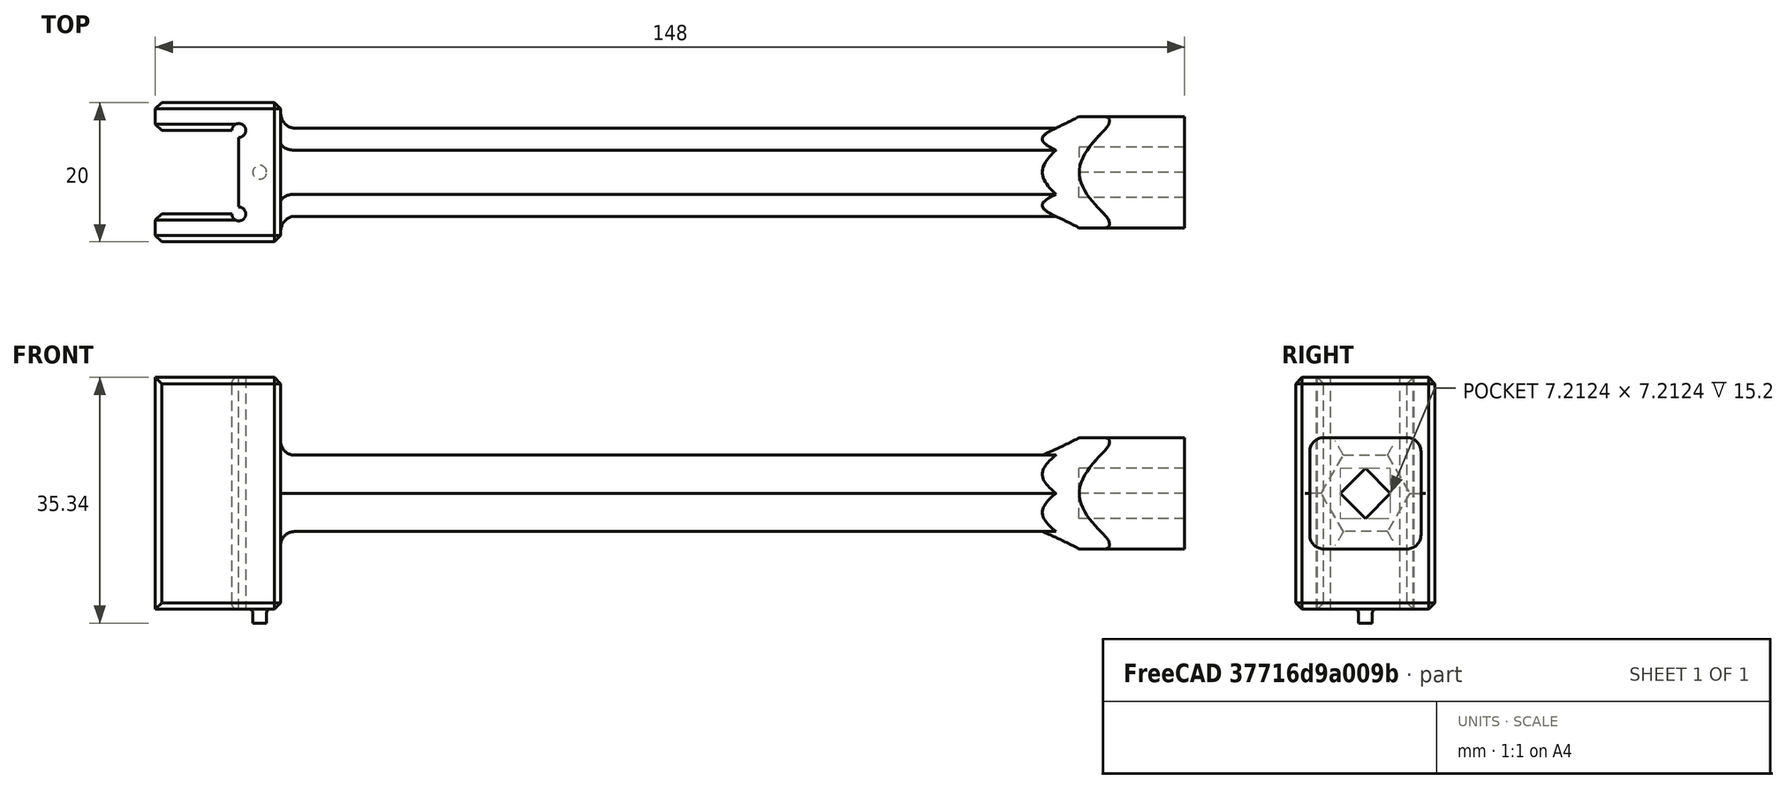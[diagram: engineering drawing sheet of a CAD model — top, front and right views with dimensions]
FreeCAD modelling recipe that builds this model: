
FCSTD DOCUMENT  (FreeCAD 0.21R33771 (Git))
Label: wrench
License: All rights reserved
LicenseURL: http://en.wikipedia.org/wiki/All_rights_reserved
objects: Sketcher::SketchObject×8, PartDesign::Pad×4, PartDesign::Fillet×3, PartDesign::Pocket×3, Spreadsheet::Sheet×1, PartDesign::Plane×1, PartDesign::Revolution×1, PartDesign::Chamfer×1, PartDesign::Body×1, Mesh::Feature×1
note: 34 computed .brp shape members not serialized (recipe doc carries the construction recipe); baked Part::Feature solids carry a one-line shape summary decoded from their .brp

FEATURE [Spreadsheet::Sheet] Spreadsheet
  cells = A1='magnet width [mm]; B1=12; A2='manget lenght [mm]; B2=50; A3='holder wall thickness; B3=2
FEATURE [Sketcher::SketchObject] Sketch
  FullyConstrained = false
  MapMode = 5
  Support = -> [XY_Plane]
  expr: Constraints[13] = Spreadsheet.B1 / 3
  expr: Constraints[15] = Spreadsheet.B1
  expr: Constraints[25] = Spreadsheet.B1 / 2
  sketch-geometry (21):
    g0: LineSegment StartX=-6 StartY=6 StartZ=0 EndX=-6 EndY=10 EndZ=0
    g1: LineSegment StartX=-6 StartY=10 StartZ=0 EndX=12 EndY=10 EndZ=0
    g2: LineSegment StartX=12 StartY=10 StartZ=0 EndX=12 EndY=-10 EndZ=0
    g3: LineSegment StartX=12 StartY=-10 StartZ=0 EndX=-6 EndY=-10 EndZ=0
    g4: LineSegment StartX=-6 StartY=-10 StartZ=0 EndX=-6 EndY=-6 EndZ=0
    g5: LineSegment StartX=-6 StartY=-6 StartZ=0 EndX=6 EndY=-6 EndZ=0
    g6: LineSegment StartX=6 StartY=-6 StartZ=0 EndX=6 EndY=6 EndZ=0
    g7: LineSegment StartX=6 StartY=6 StartZ=0 EndX=-6 EndY=6 EndZ=0
    g8: LineSegment StartX=-6 StartY=6 StartZ=0 EndX=6 EndY=-6 EndZ=0
    g9: LineSegment StartX=6 StartY=6 StartZ=0 EndX=-6 EndY=-6 EndZ=0
    g10: LineSegment StartX=-6 StartY=6 StartZ=0 EndX=5.2 EndY=6 EndZ=0
    g11: LineSegment StartX=6 StartY=6 StartZ=0 EndX=6 EndY=-6 EndZ=0
    g12: LineSegment StartX=-6 StartY=-6 StartZ=0 EndX=5.2 EndY=-6 EndZ=0
    g13: LineSegment StartX=-6 StartY=-6 StartZ=0 EndX=-3 EndY=-6 EndZ=0
    g14: LineSegment StartX=-6 StartY=-7 StartZ=0 EndX=-6 EndY=-6 EndZ=0
    g15: LineSegment StartX=-6 StartY=6 StartZ=0 EndX=-3 EndY=6 EndZ=0
    g16: LineSegment StartX=-6 StartY=7 StartZ=0 EndX=-6 EndY=6 EndZ=0
    g17: LineSegment StartX=-6 StartY=6 StartZ=0 EndX=-6 EndY=10 EndZ=0
    g18: LineSegment StartX=-6 StartY=-6 StartZ=0 EndX=-6 EndY=-10 EndZ=0
    g19: LineSegment StartX=-6 StartY=6 StartZ=0 EndX=6 EndY=6 EndZ=0
    g20: LineSegment StartX=-6 StartY=-6 StartZ=0 EndX=6 EndY=-6 EndZ=0
  constraints (49):
    c: Coincident(g1,g0)
    c: Horizontal(g1)
    c: Coincident(g2,g1)
    c: Vertical(g2)
    c: Coincident(g3,g2)
    c: Horizontal(g3)
    c: Coincident(g4,g3)
    c: Coincident(g5,g4)
    c: Horizontal(g5)
    c: Coincident(g7,g0)
    c: Horizontal(g7)
    c: Coincident(g5,g6)
    c: Coincident(g6,g7)
    c: Distance(g6,g1) = 4
    c: Equal(g0,g4)
    c: Distance(g4,g7) = 12
    c: Coincident(g8,g0)
    c: Coincident(g8,g5)
    c: PointOnObject(g-1,g8)
    c: Tangent(g0,g4)
    c: Vertical(g0)
    c: Coincident(g9,g6)
    c: Coincident(g9,g4)
    c: PointOnObject(g-1,g9)
    c: Equal(g7,g6)
    c: Distance(g5,g2) = 6
    c: Coincident(g10,g0)
    c: PointOnObject(g10,g7)
    c: Coincident(g12,g4)
    c: PointOnObject(g12,g5)
    c: Coincident(g14,g13)
    c: Horizontal(g13)
    c: Vertical(g14)
    c: Coincident(g13,g4)
    c: Coincident(g16,g15)
    c: Horizontal(g15)
    c: Vertical(g16)
    c: Coincident(g15,g0)
    c: Coincident(g17,g1)
    c: Coincident(g18,g3)
    c: Coincident(g17,g0)
    c: Coincident(g19,g17)
    c: Coincident(g18,g4)
    c: Coincident(g20,g18)
    c: Coincident(g19,g6)
    c: Coincident(g11,g19)
    c: Coincident(g20,g5)
    c: Coincident(g11,g20)
    c: Vertical(g11)
FEATURE [PartDesign::Pad] Pad  label="wrench"
  Direction = (0,0,1)
  Length = 16.6667
  Length2 = 16.6667
  Profile = -> Sketch
  ReferenceAxis = -> Sketch [N_Axis]
  Type = 4
  expr: Length = Spreadsheet.B2 * 2 / 6
  expr: Length2 = Spreadsheet.B2 * 2 / 6
FEATURE [PartDesign::Plane] DatumPlane
  AttachmentOffset = pos=(0,0,7) rot=(0,0,1;0rad)
  Length = 60
  MapMode = 5
  Placement = pos=(7,-1.6e-15,1.6e-15) rot=(0.57735,0.57735,0.57735;2.0944rad)
  ResizeMode = 0
  Support = -> [YZ_Plane]
  Width = 60
  expr: .AttachmentOffset.Base.z = Spreadsheet.B1 / 2 + 1
FEATURE [Sketcher::SketchObject] Sketch001
  FullyConstrained = true
  MapMode = 5
  Placement = pos=(7,-1.6e-15,1.6e-15) rot=(0.57735,0.57735,0.57735;2.0944rad)
  Support = -> [DatumPlane]
  sketch-geometry (7):
    g0: LineSegment StartX=3.17543 StartY=5.5 StartZ=0 EndX=-3.17543 EndY=5.5 EndZ=0
    g1: LineSegment StartX=-3.17543 StartY=5.5 StartZ=0 EndX=-6.35085 EndY=0 EndZ=0
    g2: LineSegment StartX=-6.35085 StartY=0 StartZ=0 EndX=-3.17543 EndY=-5.5 EndZ=0
    g3: LineSegment StartX=-3.17543 StartY=-5.5 StartZ=0 EndX=3.17543 EndY=-5.5 EndZ=0
    g4: LineSegment StartX=3.17543 StartY=-5.5 StartZ=0 EndX=6.35085 EndY=-9e-16 EndZ=0
    g5: LineSegment StartX=6.35085 StartY=-9e-16 StartZ=0 EndX=3.17543 EndY=5.5 EndZ=0
    g6: Circle CenterX=0 CenterY=0 CenterZ=0 NormalX=0 NormalY=0 NormalZ=1 AngleXU=0 Radius=6.35085
  constraints (16):
    c: Coincident(g0,g1)
    c: Coincident(g1,g2)
    c: Coincident(g2,g3)
    c: Coincident(g3,g4)
    c: Coincident(g4,g5)
    c: Coincident(g5,g0)
    c: Equal(g0, g1-g5) x5
    c: PointOnObject(g0,g6)
    c: PointOnObject(g1,g6)
    c: PointOnObject(g2,g6)
    c: PointOnObject(g3,g6)
    c: PointOnObject(g4,g6)
    c: PointOnObject(g5,g6)
    c: Horizontal(g0)
    c: Distance(g0,g3) = 11
    c: Coincident(g6,g-1)
FEATURE [PartDesign::Pad] Pad001  label="handle"
  BaseFeature = -> Pad
  Direction = (1,-1e-16,1e-16)
  Length = 130
  Length2 = 10
  Profile = -> Sketch001
  ReferenceAxis = -> Sketch001 [N_Axis]
  Type = 0
FEATURE [Sketcher::SketchObject] Sketch005
  FullyConstrained = false
  MapMode = 5
  Support = -> [XY_Plane]
  expr: Constraints[2] = Spreadsheet.B1 * sqrt(2) / 2 + Spreadsheet.B3 + 4
  sketch-geometry (5):
    g0: LineSegment StartX=137 StartY=0 StartZ=0 EndX=137 EndY=14.4853 EndZ=0
    g1: LineSegment StartX=137 StartY=14.4853 StartZ=0 EndX=94.3606 EndY=70 EndZ=0
    g2: ArcOfCircle CenterX=94.3606 CenterY=70 CenterZ=0 NormalX=0 NormalY=0 NormalZ=1 AngleXU=0 Radius=70 StartAngle=4.71239 EndAngle=5.36736
    g3: LineSegment StartX=94.3606 StartY=0 StartZ=0 EndX=94.3606 EndY=70 EndZ=0
    g4: LineSegment StartX=94.3606 StartY=0 StartZ=0 EndX=137 EndY=0 EndZ=0
  constraints (13):
    c: Vertical(g0)
    c: PointOnObject(g0,g-1)
    c: DistanceY(g0,g0) = 14.4853
    c: Coincident(g1,g0)
    c: Coincident(g2,g1)
    c: Coincident(g2,g0)
    c: Coincident(g3,g2)
    c: Coincident(g3,g2)
    c: Coincident(g4,g2)
    c: Coincident(g4,g0)
    c: Horizontal(g4)
    c: Vertical(g3)
    c: DistanceY(g2) = 70
FEATURE [Sketcher::SketchObject] Sketch002
  FullyConstrained = true
  MapMode = 5
  Placement = pos=(137,0,2.2e-14) rot=(0.57735,0.57735,0.57735;2.0944rad)
  expr: Constraints[10] = Spreadsheet.B1 + Spreadsheet.B3 * 2
  sketch-geometry (5):
    g0: LineSegment StartX=-8 StartY=-8 StartZ=0 EndX=-8 EndY=8 EndZ=0
    g1: LineSegment StartX=-8 StartY=8 StartZ=0 EndX=8 EndY=8 EndZ=0
    g2: LineSegment StartX=8 StartY=8 StartZ=0 EndX=8 EndY=-8 EndZ=0
    g3: LineSegment StartX=8 StartY=-8 StartZ=0 EndX=-8 EndY=-8 EndZ=0
    g4: GeomPoint X=0 Y=0 Z=0
  constraints (12):
    c: Coincident(g0,g1)
    c: Coincident(g1,g2)
    c: Coincident(g2,g3)
    c: Coincident(g3,g0)
    c: Horizontal(g1)
    c: Horizontal(g3)
    c: Vertical(g0)
    c: Vertical(g2)
    c: Symmetric(g1,g0,g4)
    c: Coincident(g4,g-1)
    c: Distance(g1,g2) = 16
    c: Equal(g2,g3)
FEATURE [PartDesign::Pad] Pad002  label="holder body"
  BaseFeature = -> Pad001
  Direction = (1,0,0)
  Length = 5
  Length2 = 10
  Profile = -> Sketch002
  ReferenceAxis = -> Sketch002 [N_Axis]
  Type = 0
FEATURE [PartDesign::Fillet] Fillet001  label="wrench fillets"
  Base = -> Pad002 [Edge24,Edge26,Edge28,Edge30,Edge19,Edge22]
  BaseFeature = -> Pad002
  Radius = 2
  SupportTransform = false
  UseAllEdges = false
FEATURE [PartDesign::Fillet] Fillet002  label="holder outer fillets"
  Base = -> Fillet001 [Edge37,Edge39,Edge34,Edge35]
  BaseFeature = -> Fillet001
  Radius = 2
  SupportTransform = false
  UseAllEdges = false
  expr: Radius = Spreadsheet.B3
FEATURE [PartDesign::Revolution] Revolution  label="rounden rod to holder"
  Angle = 360
  Axis = (1,0,0)
  Base = (0,0,0)
  BaseFeature = -> Fillet002
  Profile = -> Sketch005
  ReferenceAxis = -> Sketch005 [H_Axis]
FEATURE [Sketcher::SketchObject] Sketch006
  FullyConstrained = false
  MapMode = 5
  Placement = pos=(137,0,0) rot=(0.57735,0.57735,0.57735;2.0944rad)
  Support = -> [Revolution]
  expr: Constraints[22] = Spreadsheet.B1 + Spreadsheet.B3 * 2
  expr: Constraints[34] = Spreadsheet.B1 + Spreadsheet.B3 * 2 - 4
  sketch-geometry (23):
    g0: LineSegment StartX=-35 StartY=-35 StartZ=0 EndX=-35 EndY=35 EndZ=0
    g1: LineSegment StartX=-35 StartY=35 StartZ=0 EndX=35 EndY=35 EndZ=0
    g2: LineSegment StartX=35 StartY=35 StartZ=0 EndX=35 EndY=-35 EndZ=0
    g3: LineSegment StartX=35 StartY=-35 StartZ=0 EndX=-35 EndY=-35 EndZ=0
    g4: GeomPoint X=0 Y=0 Z=0
    g5: LineSegment StartX=-8 StartY=-8 StartZ=0 EndX=-8 EndY=8 EndZ=0
    g6: LineSegment StartX=-8 StartY=8 StartZ=0 EndX=8 EndY=8 EndZ=0
    g7: LineSegment StartX=8 StartY=8 StartZ=0 EndX=8 EndY=-8 EndZ=0
    g8: LineSegment StartX=8 StartY=-8 StartZ=0 EndX=-8 EndY=-8 EndZ=0
    g9: GeomPoint X=0 Y=0 Z=0
    g10: LineSegment StartX=-6 StartY=-6 StartZ=0 EndX=-6 EndY=6 EndZ=0
    g11: LineSegment StartX=-6 StartY=6 StartZ=0 EndX=6 EndY=6 EndZ=0
    g12: LineSegment StartX=6 StartY=6 StartZ=0 EndX=6 EndY=-6 EndZ=0
    g13: LineSegment StartX=6 StartY=-6 StartZ=0 EndX=-6 EndY=-6 EndZ=0
    g14: GeomPoint X=0 Y=0 Z=0
    g15: ArcOfCircle CenterX=-6 CenterY=6 CenterZ=0 NormalX=0 NormalY=0 NormalZ=1 AngleXU=0 Radius=2 StartAngle=1.5708 EndAngle=3.14159
    g16: ArcOfCircle CenterX=6 CenterY=6 CenterZ=0 NormalX=0 NormalY=0 NormalZ=1 AngleXU=0 Radius=2 StartAngle=2.09637e-08 EndAngle=1.5708
    g17: ArcOfCircle CenterX=6 CenterY=-6 CenterZ=0 NormalX=0 NormalY=0 NormalZ=1 AngleXU=0 Radius=2 StartAngle=4.71239 EndAngle=6.28319
    g18: ArcOfCircle CenterX=-6 CenterY=-6 CenterZ=0 NormalX=0 NormalY=0 NormalZ=1 AngleXU=0 Radius=2 StartAngle=3.14159 EndAngle=4.71239
    g19: LineSegment StartX=-6 StartY=8 StartZ=0 EndX=6 EndY=8 EndZ=0
    g20: LineSegment StartX=8 StartY=6 StartZ=0 EndX=8 EndY=-6 EndZ=0
    g21: LineSegment StartX=6 StartY=-8 StartZ=0 EndX=-6 EndY=-8 EndZ=0
    g22: LineSegment StartX=-8 StartY=-6 StartZ=0 EndX=-8 EndY=6 EndZ=0
  constraints (55):
    c: Coincident(g0,g1)
    c: Coincident(g1,g2)
    c: Coincident(g2,g3)
    c: Coincident(g3,g0)
    c: Horizontal(g1)
    c: Horizontal(g3)
    c: Vertical(g0)
    c: Vertical(g2)
    c: Symmetric(g1,g0,g4)
    c: Coincident(g4,g-1)
    c: Equal(g2,g3)
    c: Distance(g1,g2) = 70
    c: Coincident(g5,g6)
    c: Coincident(g6,g7)
    c: Coincident(g7,g8)
    c: Coincident(g8,g5)
    c: Horizontal(g8)
    c: Vertical(g5)
    c: Vertical(g7)
    c: Symmetric(g6,g5,g9)
    c: Coincident(g9,g4)
    c: Equal(g7,g8)
    c: Distance(g6,g7) = 16
    c: Coincident(g10,g11)
    c: Coincident(g11,g12)
    c: Coincident(g12,g13)
    c: Coincident(g13,g10)
    c: Horizontal(g11)
    c: Horizontal(g13)
    c: Vertical(g10)
    c: Vertical(g12)
    c: Symmetric(g11,g10,g14)
    c: Coincident(g14,g4)
    c: Equal(g12,g13)
    c: Distance(g11,g12) = 12
    c: Coincident(g15,g10)
    c: PointOnObject(g15,g6)
    c: Tangent(g15,g5) = 1.5708
    c: Coincident(g16,g11)
    c: PointOnObject(g16,g7)
    c: Tangent(g16,g6) = 1.5708
    c: Coincident(g17,g12)
    c: PointOnObject(g17,g8)
    c: Tangent(g17,g7) = 1.5708
    c: Tangent(g18,g8) = 1.5708
    c: Coincident(g18,g10)
    c: Coincident(g19,g15)
    c: Coincident(g19,g16)
    c: Coincident(g20,g16)
    c: Vertical(g20)
    c: Coincident(g21,g17)
    c: Coincident(g21,g18)
    c: Coincident(g22,g18)
    c: Vertical(g22)
    c: Coincident(g22,g15)
FEATURE [PartDesign::Pocket] Pocket002  label="cut down to holder"
  BaseFeature = -> Revolution
  Direction = (-1,0,0)
  Length = 21
  Length2 = 5
  Profile = -> Sketch006
  ReferenceAxis = -> Sketch006 [N_Axis]
  Type = 0
FEATURE [Sketcher::SketchObject] Sketch007
  FullyConstrained = true
  MapMode = 5
  Placement = pos=(142,0,0) rot=(0.57735,0.57735,0.57735;2.0944rad)
  Support = -> [Pocket002]
  sketch-geometry (13):
    g0: LineSegment StartX=3.17543 StartY=5.5 StartZ=0 EndX=-3.17543 EndY=5.5 EndZ=0
    g1: LineSegment StartX=-3.17543 StartY=5.5 StartZ=0 EndX=-6.35085 EndY=1.40936e-11 EndZ=0
    g2: LineSegment StartX=-6.35085 StartY=1.40936e-11 StartZ=0 EndX=-3.17543 EndY=-5.5 EndZ=0
    g3: LineSegment StartX=-3.17543 StartY=-5.5 StartZ=0 EndX=3.17543 EndY=-5.5 EndZ=0
    g4: LineSegment StartX=3.17543 StartY=-5.5 StartZ=0 EndX=6.35085 EndY=1.40936e-11 EndZ=0
    g5: LineSegment StartX=6.35085 StartY=1.40936e-11 StartZ=0 EndX=3.17543 EndY=5.5 EndZ=0
    g6: Circle CenterX=0 CenterY=0 CenterZ=0 NormalX=0 NormalY=0 NormalZ=1 AngleXU=0 Radius=6.35085
    g7: LineSegment StartX=0 StartY=3.60624 StartZ=0 EndX=3.60624 EndY=0 EndZ=0
    g8: LineSegment StartX=3.60624 StartY=0 StartZ=0 EndX=0 EndY=-3.60624 EndZ=0
    g9: LineSegment StartX=0 StartY=-3.60624 StartZ=0 EndX=-3.60624 EndY=-4e-16 EndZ=0
    g10: LineSegment StartX=-3.60624 StartY=-4e-16 StartZ=0 EndX=0 EndY=3.60624 EndZ=0
    g11: LineSegment StartX=0 StartY=3.60624 StartZ=0 EndX=0 EndY=-3.60624 EndZ=0
    g12: LineSegment StartX=3.60624 StartY=0 StartZ=0 EndX=-3.60624 EndY=-4e-16 EndZ=0
  constraints (32):
    c: Coincident(g0,g1)
    c: Coincident(g1,g2)
    c: Coincident(g2,g3)
    c: Coincident(g3,g4)
    c: Coincident(g4,g5)
    c: Coincident(g5,g0)
    c: Equal(g0, g1-g5) x5
    c: PointOnObject(g0,g6)
    c: PointOnObject(g1,g6)
    c: PointOnObject(g2,g6)
    c: PointOnObject(g3,g6)
    c: PointOnObject(g4,g6)
    c: PointOnObject(g5,g6)
    c: Coincident(g6,g-1)
    c: Horizontal(g0)
    c: Distance(g0,g3) = 11
    c: PointOnObject(g7,g-2)
    c: PointOnObject(g7,g-1)
    c: Coincident(g8,g7)
    c: PointOnObject(g8,g-2)
    c: Coincident(g9,g8)
    c: PointOnObject(g9,g-1)
    c: Coincident(g10,g9)
    c: Coincident(g10,g7)
    c: Coincident(g11,g7)
    c: Coincident(g11,g8)
    c: Coincident(g12,g7)
    c: Coincident(g12,g9)
    c: Equal(g7,g8)
    c: Equal(g7,g9)
    c: Equal(g11,g12)
    c: Distance(g9,g7) = 5.1
FEATURE [PartDesign::Pocket] Pocket  label="groove"
  BaseFeature = -> Pocket002
  Direction = (-1,0,0)
  Length = 15.2
  Length2 = 5
  Profile = -> Sketch007
  ReferenceAxis = -> Sketch007 [N_Axis]
  Type = 0
FEATURE [Sketcher::SketchObject] Sketch008
  ExternalGeometry = -> [Pocket]
  FullyConstrained = true
  MapMode = 5
  Placement = pos=(0,0,-16.6667) rot=(1,0,0;3.14159rad)
  Support = -> [Pocket]
  sketch-geometry (2):
    g0: Circle CenterX=9 CenterY=0 CenterZ=0 NormalX=0 NormalY=0 NormalZ=1 AngleXU=0 Radius=1
    g1: Circle CenterX=9 CenterY=0 CenterZ=0 NormalX=0 NormalY=0 NormalZ=1 AngleXU=0 Radius=3
  constraints (5):
    c: PointOnObject(g0,g-1)
    c: Coincident(g1,g0)
    c: Tangent(g1,g-4)
    c: Tangent(g1,g-3)
    c: Radius(g0) = 1
FEATURE [PartDesign::Pad] Pad003  label="north mark"
  BaseFeature = -> Pocket
  Direction = (0,0,-1)
  Length = 2
  Length2 = 10
  Profile = -> Sketch008
  ReferenceAxis = -> Sketch008 [N_Axis]
  Type = 0
FEATURE [PartDesign::Fillet] Fillet  label="north mark Fillet"
  Base = -> Pad003 [Edge98]
  BaseFeature = -> Pad003
  Radius = 0.5
  SupportTransform = false
  UseAllEdges = false
FEATURE [Sketcher::SketchObject] Sketch009
  ExternalGeometry = -> [Fillet]
  FullyConstrained = true
  MapMode = 5
  Support = -> [XY_Plane]
  sketch-geometry (2):
    g0: Circle CenterX=6 CenterY=6 CenterZ=0 NormalX=0 NormalY=0 NormalZ=1 AngleXU=0 Radius=1
    g1: Circle CenterX=6 CenterY=-6 CenterZ=0 NormalX=0 NormalY=0 NormalZ=1 AngleXU=0 Radius=1
  constraints (4):
    c: Coincident(g0,g-3)
    c: Coincident(g1,g-3)
    c: Equal(g0,g1)
    c: Radius(g0) = 1
FEATURE [PartDesign::Pocket] Pocket003  label="wrench inner roundings"
  BaseFeature = -> Fillet
  Direction = (0,0,-1)
  Length = 5
  Length2 = 5
  Midplane = true
  Profile = -> Sketch009
  ReferenceAxis = -> Sketch009 [N_Axis]
  Type = 1
FEATURE [PartDesign::Chamfer] Chamfer  label="wrench outer chamfers"
  Angle = 45
  Base = -> Pocket003 [Edge2,Edge3,Edge4,Edge6,Edge12,Edge18,Edge15,Edge14,Edge29,Edge27,Edge32,Edge43,Edge25,Edge28,Edge26,Edge17]
  BaseFeature = -> Pocket003
  ChamferType = 0
  FlipDirection = false
  Size = 0.9
  Size2 = 1
  SupportTransform = false
  UseAllEdges = false
FEATURE [PartDesign::Body] Body
  Group = -> [Sketch,Pad,DatumPlane,Sketch001,Pad001,Sketch002,Pad002,Fillet001,Fillet002,Sketch005,Revolution,Sketch006,Pocket002,Sketch007,Pocket,Sketch008,Pad003,Fillet,Sketch009,Pocket003,Chamfer]
  Origin = -> Origin
  Tip = -> Chamfer
FEATURE [Mesh::Feature] Mesh  label="print-wrench"
